# Revit family: 1396xxx Can 50 Recessed
name_source: partatom
category: Lighting Fixtures
units: mm (PartAtom-declared; Revit-internal decimal feet)

## family parameters
Always vertical = Yes
Cut with Voids When Loaded = No
Host = Ceiling
Light Source = Yes
OmniClass Number = 23.80.70.11
OmniClass Title = Luminaries for Internal Lighting
Part Type = Normal
Room Calculation Point = No
Round Connector Dimension = Use Diameter
Shared = No

## types (2) — shared parameters
Color Filter = 16777215
Dimmable = Yes
Dimming Lamp Color Temperature Shift = <None>
Dimming Method = Phase - Leading and Trailing Edge
Driver Included = Yes (Integral)
Driver Required = No
Efficacy (lm/w) = 62
Electrical Class = 1
Emit Shape Visible in Rendering = No
Emit from Circle Diameter = 1 mm  [stored 0.00328084 ft]
Lamp = LED
Light Source Fixed = No
Main Finish = Various
Main Material = Metal - Aluminium
Manufacturer URL - Europe and Rest of World = www.astrolighting.com
Manufacturer URL - North America = us.astrolighting.com
Photometric Web File = 1396024_Can 50 Single Matt White_Photometry_IES_Iss.01.ies
Power (Watts) = 8.2
Product CCT = 3000K
Product Dimensions (MM) = 133 x Ø80
zero-valued in all types: Default Elevation, Product Weight (KG)

## per-type parameters (varying)
| type | ADA compliant | Location / IP Rating | Product CRI | Product Location | Product Name | Product SKU | Tilt Angle |
| CE | Not Applicable | IP20 | 90 | Architectural / Indoor | Can 50 Recessed | 1396xxx | 0.00° |
| ETL |  |  | 80/ 90 |  |  | 1234567 | 60.00° |

note: [stored X ft] marks values corroborated as IEEE doubles in the binary element streams (Revit-internal decimal feet)

## geometry (parser evidence)
native form markers: Sweep x3
no freeform markers — native parametric forms only
